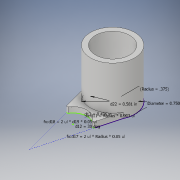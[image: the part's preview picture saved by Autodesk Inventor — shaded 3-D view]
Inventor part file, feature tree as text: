
AUTODESK INVENTOR PART (.ipt)
format: ipt  version: 2018.3 (Build 223284000, 284)  size: 137,216 bytes
history: native  units: in
note: dims shown in document units (in); Inventor stores cm internally (conversion verified against a paired STEP export)
features: extrude x3, sketch x1
ambient origin geometry x8: Origin, YZ Plane, XZ Plane, XY Plane, X Axis, Y Axis, Z Axis, Center Point
bodies: Solid1 (feature_tree)
feature tree (4):
  sketch  "Sketch1"  dims[d11=0.3386in d12=30.0deg d13=0.436in d17=0.0375in d18=0.0375in d19=0.375in d20=0.091in d21=0.0in d22=0.581in d23=0.5625in d24=0.0in d25=0.8281in d26=0.0in]
  extrude  "Extrusion1"  TaperAngle=30.0deg  [1 undecoded]
  extrude  "Extrusion2"  Depth=0.8281in
  extrude  "Extrusion3"  Depth=0.8281in
note: 1 required parameter value undecoded (feature->parameter linkage not recoverable at this tier; creation-order binding heuristic only, values carry confidence <= 0.55)
